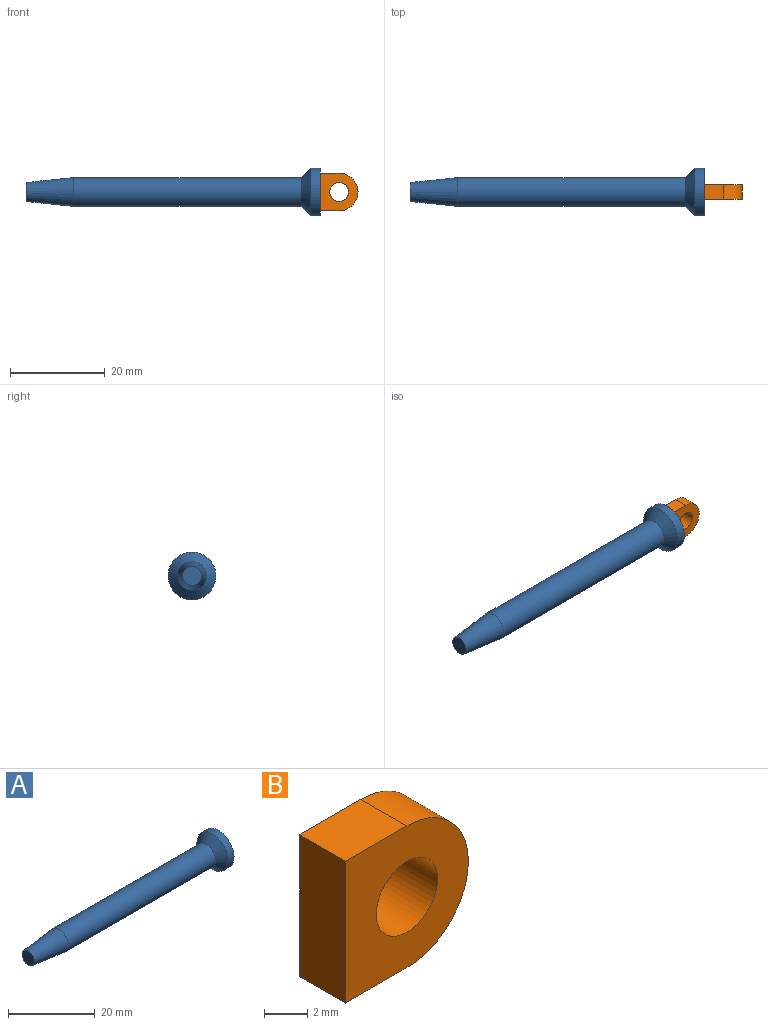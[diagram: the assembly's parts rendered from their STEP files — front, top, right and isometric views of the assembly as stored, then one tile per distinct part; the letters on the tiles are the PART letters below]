
ASSEMBLY  parts=2 mates=1
PART A: 6 faces, bbox 62.1x10.1x10.1 mm
  f0: cylinder r=5.05mm len=10.1mm, axis (1,0,0), area 63.5mm2, adj f1,f5
  f1: cone r=5.05mm half-angle=45deg, axis (1,0,0), area 72mm2, adj f0,f2
  f2: cylinder r=3.05mm len=48mm, axis (1,0,0), area 919.9mm2, adj f1,f3
  f3: cone r=3.05mm half-angle=5.9deg, axis (1,0,0), area 161.1mm2, adj f2,f4
  f4: plane 4x4mm, normal (-1,0,0), area 12.6mm2, adj f3
  f5: plane 10.1x10.1mm, normal (1,0,0), area 80.1mm2, adj f0
PART B: 7 faces, bbox 8x3x8 mm
  f0: plane 8x3mm, normal (-1,0,0), area 24mm2, adj f1,f3,f5,f6
  f1: plane 4x3mm, normal (0,0,-1), area 12mm2, adj f0,f2,f5,f6
  f2: cylinder r=4mm len=8mm, axis (0,1,0), area 37.7mm2, adj f1,f3,f5,f6
  f3: plane 4x3mm, normal (0,0,1), area 12mm2, adj f0,f2,f5,f6
  f4: cylinder r=2mm len=4mm, axis (0,1,0), area 37.7mm2, adj f5,f6
  f5: plane 8x8mm, normal (0,-1,0), area 44.5mm2, adj f0,f1,f2,f3,f4
  f6: plane 8x8mm, normal (0,1,0), area 44.5mm2, adj f0,f1,f2,f3,f4
PLACE A t=(2.53,7.98,-5.17)mm
PLACE B t=(49.09,9.48,-28.39)mm
MATE fastened A.f1 <-> B.f0  axis (1,0,0) through (-10.28,7.98,12.06)mm
